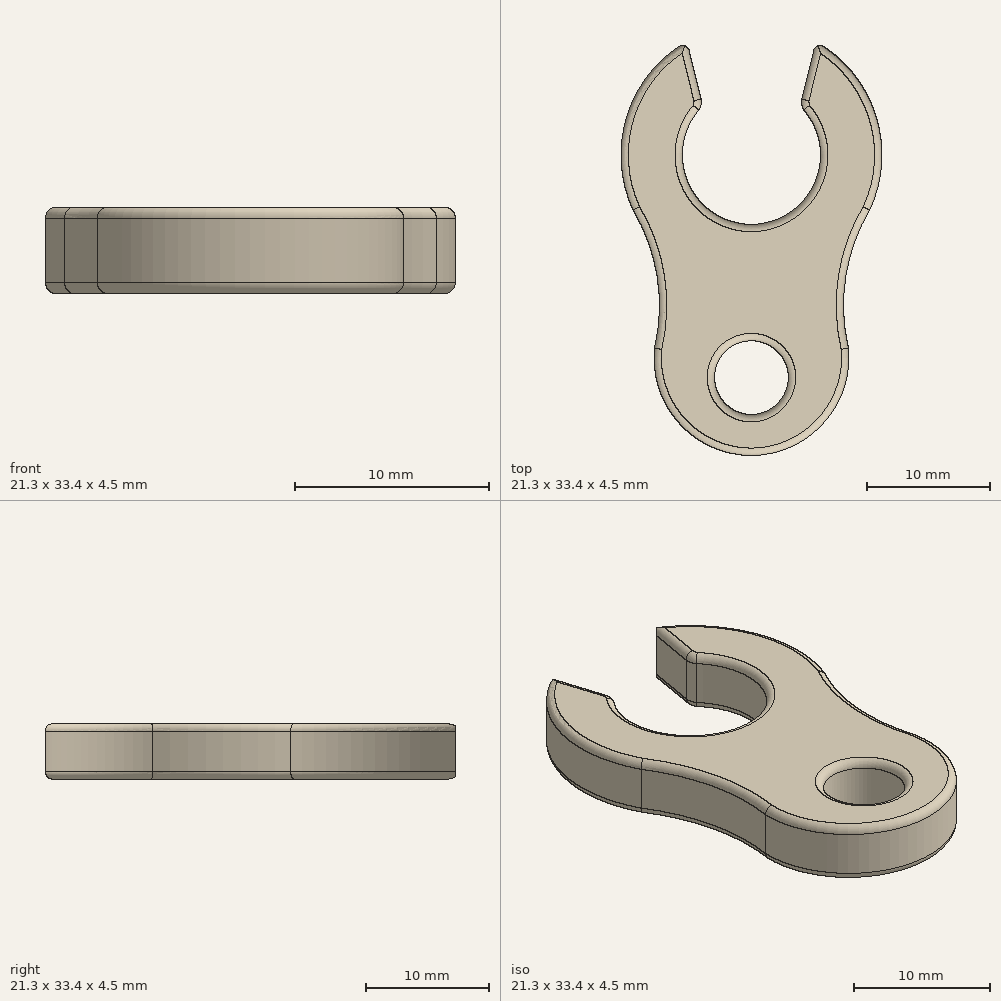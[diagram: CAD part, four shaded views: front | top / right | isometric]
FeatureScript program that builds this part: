
annotation { "Feature Type Name" : "Feature", "Feature Type Description" : "" }
export const myFeature = defineFeature(function(context is Context, id is Id, definition is map)
    precondition{}
    {
        {
            var Q0;
            Q0=qCreatedBy(makeId("Top.planeOp"),FACE);
            var sketch = newSketch(context, id + "F0", { "sketchPlane" : qUnion([Q0])});
            skArc(sketch, "E0", {"start": v(-4.25, 3.68) * mm, "mid": v(0, -5.63) * mm, "end": v(4.25, 3.68) * mm});
            skArc(sketch, "E1.0", {"start": v(-5.81, 8.9) * mm, "mid": v(-10.22, 2.92) * mm, "end": v(-9.64, -4.48) * mm});
            skLineSegment(sketch, "E2", {"start": v(-4.1, 4.57) * mm, "end": v(-5.1, 8.6) * mm});
            skLineSegment(sketch, "E3.0.MirrorCS", {"start": v(4.1, 4.57) * mm, "end": v(5.1, 8.6) * mm});
            skArc(sketch, "E4", {"start": v(-7.64, -14.38) * mm, "mid": v(0, -24.44) * mm, "end": v(7.64, -14.38) * mm});
            skArc(sketch, "E5.trimOffspring", {"start": v(9.64, -4.48) * mm, "mid": v(10.22, 2.92) * mm, "end": v(5.81, 8.9) * mm});
            skArc(sketch, "E6", {"start": v(-7.9, -15.7) * mm, "mid": v(-7.67, -9.92) * mm, "end": v(-9.64, -4.48) * mm});
            skArc(sketch, "E7.0.MirrorCS", {"start": v(7.9, -15.7) * mm, "mid": v(7.67, -9.92) * mm, "end": v(9.64, -4.48) * mm});
            skCircle(sketch, "E8", {"center": v(0, -18.1) * mm, "radius": 3 * mm});
            skArc(sketch, "E9", {"start": v(-4.25, 3.68) * mm, "mid": v(-4.1, 4.11) * mm, "end": v(-4.1, 4.57) * mm});
            skPoint(sketch, "E10.orphan", {"position": v(-3.96, 4) * mm});
            skArc(sketch, "E11.0.MirrorCS", {"start": v(4.25, 3.68) * mm, "mid": v(4.1, 4.11) * mm, "end": v(4.1, 4.57) * mm});
            skPoint(sketch, "E12.orphan", {"position": v(3.96, 4) * mm});
            skArc(sketch, "E13", {"start": v(-5.1, 8.6) * mm, "mid": v(-5.4, 8.9) * mm, "end": v(-5.81, 8.9) * mm});
            skPoint(sketch, "E14.orphan", {"position": v(-5.25, 9.24) * mm});
            skArc(sketch, "E15.0.MirrorCS", {"start": v(5.1, 8.6) * mm, "mid": v(5.4, 8.9) * mm, "end": v(5.81, 8.9) * mm});
            skPoint(sketch, "E16.orphan", {"position": v(5.25, 9.24) * mm});
            skSolve(sketch);
        }
        {
            var Q0;
            {var subQ0=sQuery(id+"F0.wireOp",EDGE,"E6");var subQ1=sQuery(id+"F0.wireOp",EDGE,"E1.0");var subQ3=makeQuery(id+"F0.imprint","INTERSECT",VERTEX,{"disambiguationData":[OD(0.0)],"derivedFrom":[subQ1,subQ0]});Q0=makeQuery(id+"F0.imprint","IMPRINT",FACE,{"disambiguationData":[TD([[makeQuery(id+"F0.imprint","IMPRINT",EDGE,{"disambiguationData":[TD([[subQ3,1.0]])],"derivedFrom":subQ1}),1.0]])]});}
            var Q1;
            {var subQ0=sQuery(id+"F0.wireOp",EDGE,"E6");var subQ1=sQuery(id+"F0.wireOp",EDGE,"E4");var subQ3=makeQuery(id+"F0.imprint","INTERSECT",VERTEX,{"disambiguationData":[OD(0.0)],"derivedFrom":[subQ1,subQ0]});Q1=makeQuery(id+"F0.imprint","IMPRINT",FACE,{"disambiguationData":[TD([[makeQuery(id+"F0.imprint","IMPRINT",EDGE,{"disambiguationData":[TD([[subQ3,-1.0]])],"derivedFrom":subQ1}),1.0]])]});}
            var Q2;
            {var subQ0=sQuery(id+"F0.wireOp",EDGE,"E7.0.MirrorCS");var subQ1=sQuery(id+"F0.wireOp",EDGE,"E4");var subQ3=makeQuery(id+"F0.imprint","INTERSECT",VERTEX,{"disambiguationData":[OD(0.0)],"derivedFrom":[subQ1,subQ0]});Q2=makeQuery(id+"F0.imprint","IMPRINT",FACE,{"disambiguationData":[TD([[makeQuery(id+"F0.imprint","IMPRINT",EDGE,{"disambiguationData":[TD([[subQ3,1.0]])],"derivedFrom":subQ1}),1.0]])]});}
            var Q3;
            {var subQ0=sQuery(id+"F0.wireOp",EDGE,"E7.0.MirrorCS");var subQ1=sQuery(id+"F0.wireOp",EDGE,"E5.trimOffspring");var subQ3=makeQuery(id+"F0.imprint","INTERSECT",VERTEX,{"disambiguationData":[OD(0.0)],"derivedFrom":[subQ1,subQ0]});Q3=makeQuery(id+"F0.imprint","IMPRINT",FACE,{"disambiguationData":[TD([[makeQuery(id+"F0.imprint","IMPRINT",EDGE,{"disambiguationData":[TD([[subQ3,-1.0]])],"derivedFrom":subQ1}),1.0]])]});}
            var Q4;
            {var subQ11=sQuery(id+"F0.wireOp",EDGE,"E0");Q4=makeQuery(id+"F0.imprint","IMPRINT",FACE,{"disambiguationData":[TD([[makeQuery(id+"F0.imprint","IMPRINT",EDGE,{"derivedFrom":subQ11}),-1.0]])]});}
            extrude(context, id + "F1", {"entities" : qUnion([Q0, Q1, Q2, Q3, Q4]), "depth" : 4.5 * mm});
        }
        {
            var Q0;
            Q0=makeQuery(id+"F1.opExtrude","CAP_EDGE",EDGE,{"disambiguationData":[OSD([sQuery(id+"F0.wireOp",EDGE,"E0")])],"isStart":false});
            var Q1;
            Q1=makeQuery(id+"F1.opExtrude","CAP_EDGE",EDGE,{"disambiguationData":[OSD([sQuery(id+"F0.wireOp",EDGE,"E8")])],"isStart":false});
            var Q2;
            Q2=makeQuery(id+"F1.opExtrude","CAP_EDGE",EDGE,{"disambiguationData":[OSD([sQuery(id+"F0.wireOp",EDGE,"E3.0.MirrorCS")])],"isStart":false});
            var Q3;
            Q3=makeQuery(id+"F1.opExtrude","CAP_EDGE",EDGE,{"disambiguationData":[OSD([sQuery(id+"F0.wireOp",EDGE,"E2")])],"isStart":false});
            var Q4;
            Q4=makeQuery(id+"F1.opExtrude","CAP_EDGE",EDGE,{"disambiguationData":[OSD([sQuery(id+"F0.wireOp",EDGE,"E8")])],"isStart":true});
            var Q5;
            Q5=makeQuery(id+"F1.opExtrude","CAP_EDGE",EDGE,{"disambiguationData":[OSD([sQuery(id+"F0.wireOp",EDGE,"E0")])],"isStart":true});
            var Q6;
            Q6=makeQuery(id+"F1.opExtrude","CAP_EDGE",EDGE,{"disambiguationData":[OSD([sQuery(id+"F0.wireOp",EDGE,"E2")])],"isStart":true});
            var Q7;
            Q7=makeQuery(id+"F1.opExtrude","CAP_EDGE",EDGE,{"disambiguationData":[OSD([sQuery(id+"F0.wireOp",EDGE,"E3.0.MirrorCS")])],"isStart":true});
            var Q8;
            Q8=makeQuery(id+"F1.opExtrude","CAP_EDGE",EDGE,{"disambiguationData":[OSD([sQuery(id+"F0.wireOp",EDGE,"E6")])],"isStart":true});
            var Q9;
            Q9=makeQuery(id+"F1.opExtrude","CAP_EDGE",EDGE,{"disambiguationData":[OSD([sQuery(id+"F0.wireOp",EDGE,"E1.0")])],"isStart":true});
            var Q10;
            Q10=makeQuery(id+"F1.opExtrude","CAP_EDGE",EDGE,{"disambiguationData":[OSD([sQuery(id+"F0.wireOp",EDGE,"E4")])],"isStart":true});
            var Q11;
            Q11=makeQuery(id+"F1.opExtrude","CAP_EDGE",EDGE,{"disambiguationData":[OSD([sQuery(id+"F0.wireOp",EDGE,"E7.0.MirrorCS")])],"isStart":true});
            var Q12;
            Q12=makeQuery(id+"F1.opExtrude","CAP_EDGE",EDGE,{"disambiguationData":[OSD([sQuery(id+"F0.wireOp",EDGE,"E5.trimOffspring")])],"isStart":true});
            var Q13;
            Q13=makeQuery(id+"F1.opExtrude","CAP_EDGE",EDGE,{"disambiguationData":[OSD([sQuery(id+"F0.wireOp",EDGE,"E7.0.MirrorCS")])],"isStart":false});
            var Q14;
            Q14=makeQuery(id+"F1.opExtrude","CAP_EDGE",EDGE,{"disambiguationData":[OSD([sQuery(id+"F0.wireOp",EDGE,"E6")])],"isStart":false});
            var Q15;
            Q15=makeQuery(id+"F1.opExtrude","CAP_EDGE",EDGE,{"disambiguationData":[OSD([sQuery(id+"F0.wireOp",EDGE,"E5.trimOffspring")])],"isStart":false});
            var Q16;
            Q16=makeQuery(id+"F1.opExtrude","CAP_EDGE",EDGE,{"disambiguationData":[OSD([sQuery(id+"F0.wireOp",EDGE,"E1.0")])],"isStart":false});
            var Q17;
            Q17=makeQuery(id+"F1.opExtrude","CAP_EDGE",EDGE,{"disambiguationData":[OSD([sQuery(id+"F0.wireOp",EDGE,"E4")])],"isStart":false});
            fillet(context, id + "F2", {"entities" : qUnion([Q0, Q1, Q2, Q3, Q4, Q5, Q6, Q7, Q8, Q9, Q10, Q11, Q12, Q13, Q14, Q15, Q16, Q17]), "radius" : .6 * mm, "tangentPropagation" : true, "allowEdgeOverflow" : false});
        }
    });
